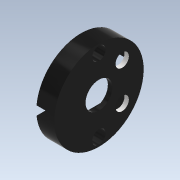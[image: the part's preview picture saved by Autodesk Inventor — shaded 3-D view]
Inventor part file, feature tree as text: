
AUTODESK INVENTOR PART (.ipt)
format: ipt  version: 2020.2 (Build 242310000, 310)  size: 171,008 bytes
history: native  units: mm
features: extrude x3, sketch x3
ambient origin geometry x8: Origin, YZ Plane, XZ Plane, XY Plane, X Axis, Y Axis, Z Axis, Center Point
bodies: Solid1 (feature_tree)
feature tree (6):
  extrude  "Extrusion1"  Depth=1.9mm
  extrude  "Extrusion2"  Depth=3.0mm
  extrude  "Extrusion3"  Depth=10.0mm
  sketch  "Sketch1"  dims[d0=20.0mm d1=1.9mm]
  sketch  "Sketch2"  dims[d2=3.0mm d3=6.0mm]
  sketch  "Sketch3"  dims[d4=1.0mm d5=0.0mm d6=5.5mm d7=6.5mm d8=5.5mm d9=11.0mm d10=3.0mm d11=6.108652mm d12=3.0mm d13=6.108652mm d14=0.2mm d15=0.2mm d16=3.0mm d17=0.0mm d18=1.0mm d19=1.0mm d20=270.0deg d21=3.5mm d22=3.5mm d23=3.0mm d24=3.0mm d25=10.0mm d26=0.0mm d27=20.0mm d29=360.0deg d31=20.0mm d33=360.0deg]
